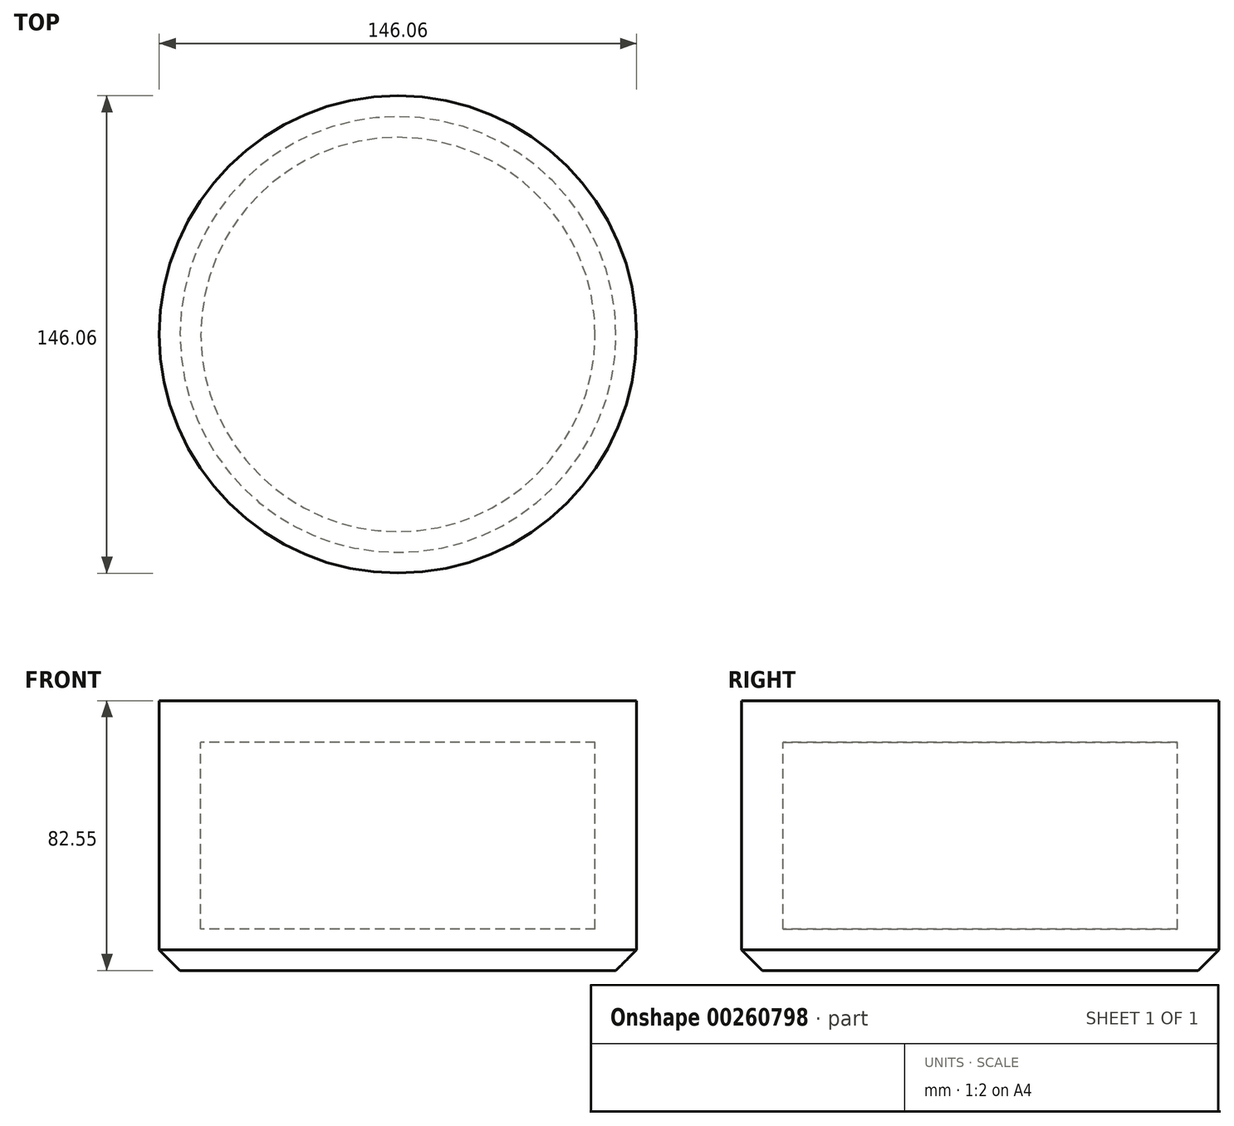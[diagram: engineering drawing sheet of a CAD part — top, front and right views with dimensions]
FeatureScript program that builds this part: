
annotation { "Feature Type Name" : "Feature", "Feature Type Description" : "" }
export const myFeature = defineFeature(function(context is Context, id is Id, definition is map)
    precondition{}
    {
        {
            var Q0;
            Q0=qCreatedBy(makeId("Top.planeOp"),FACE);
            var sketch = newSketch(context, id + "F0", { "sketchPlane" : qUnion([Q0])});
            skCircle(sketch, "E0", {"center": v(0, 0) * mm, "radius": 73.03 * mm});
            skCircle(sketch, "E1", {"center": v(0, 0) * mm, "radius": 60.33 * mm});
            skSolve(sketch);
        }
        {
            var Q0;
            Q0=makeQuery(id+"F0.imprint","IMPRINT",FACE,{"disambiguationData":[TD([[makeQuery(id+"F0.imprint","IMPRINT",EDGE,{"derivedFrom":sQuery(id+"F0.wireOp",EDGE,"E0")}),1.0]])]});
            var Q1;
            Q1=makeQuery(id+"F0.imprint","IMPRINT",FACE,{"disambiguationData":[TD([[makeQuery(id+"F0.imprint","IMPRINT",EDGE,{"derivedFrom":sQuery(id+"F0.wireOp",EDGE,"E1")}),1.0]])]});
            extrude(context, id + "F1", {"entities" : qUnion([Q0, Q1]), "oppositeDirection" : true, "depth" : 69.85 * mm});
        }
        {
            var Q0;
            Q0=makeQuery(id+"F0.imprint","IMPRINT",FACE,{"disambiguationData":[TD([[makeQuery(id+"F0.imprint","IMPRINT",EDGE,{"derivedFrom":sQuery(id+"F0.wireOp",EDGE,"E1")}),1.0]])]});
            extrude(context, id + "F2", {"entities" : qUnion([Q0]), "operationType" : NewBodyOperationType.REMOVE, "oppositeDirection" : true, "depth" : 57.15 * mm});
        }
        {
            var Q0;
            Q0=makeQuery(id+"F1.opExtrude","CAP_EDGE",EDGE,{"disambiguationData":[OSD([sQuery(id+"F0.wireOp",EDGE,"E0")])],"isStart":false});
            chamfer(context, id + "F3", {"entities" : qUnion([Q0]), "width" : 6.35 * mm, "tangentPropagation" : true});
        }
        {
            var Q0;
            Q0=makeQuery(id+"F0.imprint","IMPRINT",FACE,{"disambiguationData":[TD([[makeQuery(id+"F0.imprint","IMPRINT",EDGE,{"derivedFrom":sQuery(id+"F0.wireOp",EDGE,"E1")}),1.0]])]});
            var Q1;
            Q1=makeQuery(id+"F0.imprint","IMPRINT",FACE,{"disambiguationData":[TD([[makeQuery(id+"F0.imprint","IMPRINT",EDGE,{"derivedFrom":sQuery(id+"F0.wireOp",EDGE,"E0")}),1.0]])]});
            extrude(context, id + "F4", {"entities" : qUnion([Q0, Q1]), "operationType" : NewBodyOperationType.ADD, "depth" : 12.7 * mm});
        }
        {
            var Q0;
            Q0=makeQuery(id+"F4.opExtrude","CAP_FACE",FACE,{"disambiguationData":[OSD([sQuery(id+"F0.wireOp",EDGE,"E0")])],"isStart":false});
            extrude(context, id + "F5", {"entities" : qUnion([Q0]), "operationType" : NewBodyOperationType.ADD, "oppositeDirection" : true, "depth" : 12.7 * mm});
        }
    });
